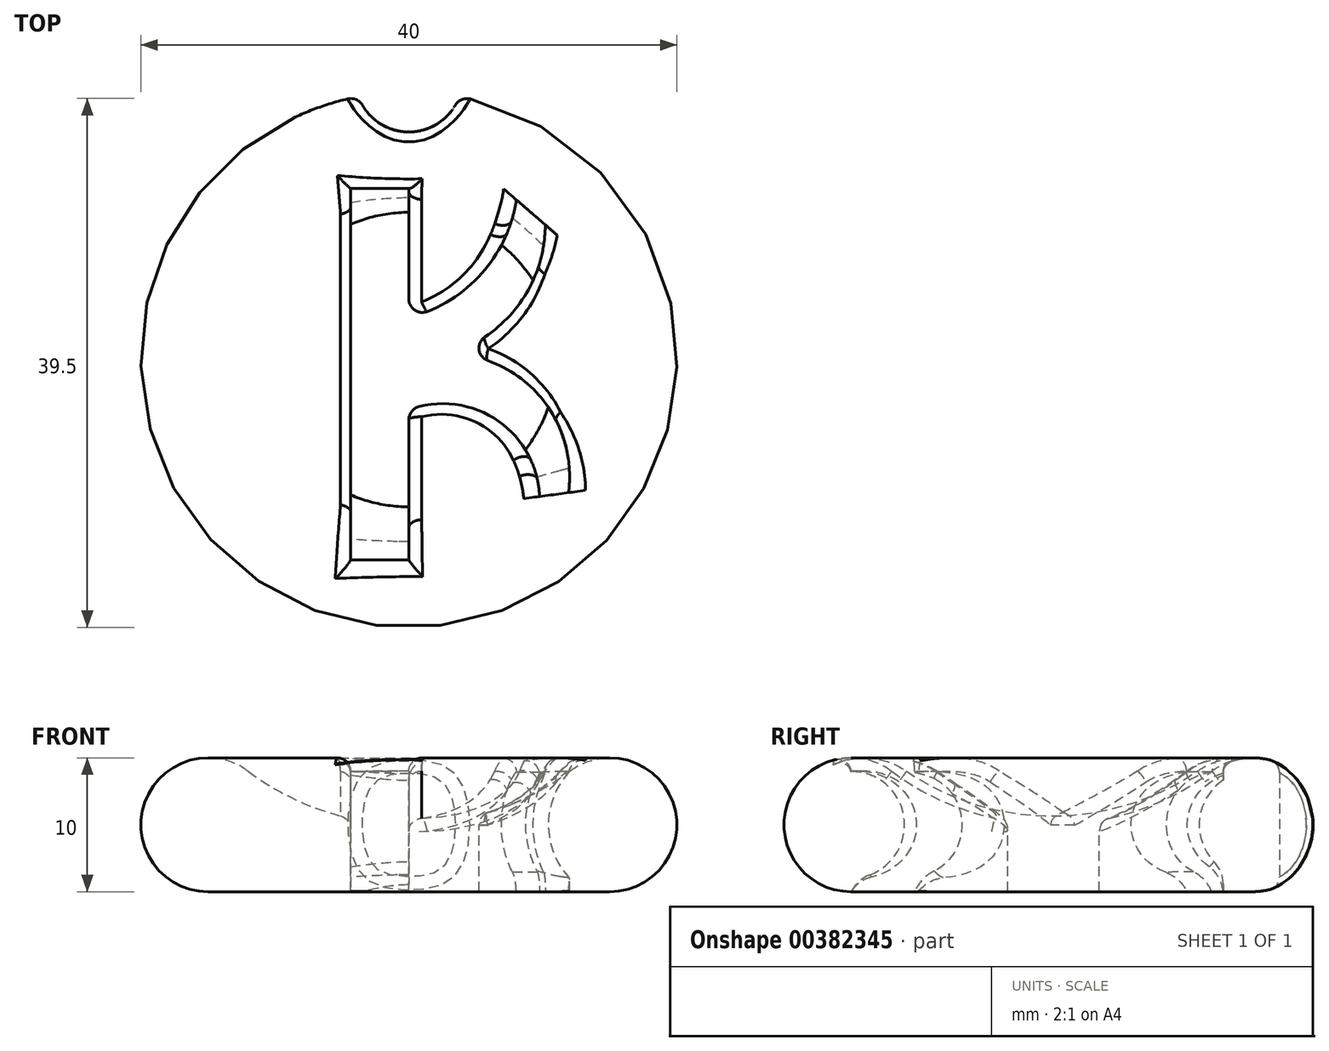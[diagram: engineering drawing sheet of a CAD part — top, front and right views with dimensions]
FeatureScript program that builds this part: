
annotation { "Feature Type Name" : "Feature", "Feature Type Description" : "" }
export const myFeature = defineFeature(function(context is Context, id is Id, definition is map)
    precondition{}
    {
        {
            var Q0;
            Q0=qCreatedBy(makeId("Front.planeOp"),FACE);
            var sketch = newSketch(context, id + "F0", { "sketchPlane" : qUnion([Q0])});
            skArc(sketch, "E0", {"start": v(-12, 9) * mm, "mid": v(-6.32, 6.03) * mm, "end": v(0, 5) * mm});
            skArc(sketch, "E1", {"start": v(-12, 9) * mm, "mid": v(-19.74, 6.58) * mm, "end": v(-15, 0) * mm});
            skLineSegment(sketch, "E2", {"start": v(-15, 0) * mm, "end": v(0, 0) * mm});
            skLineSegment(sketch, "E3", {"start": v(0, 0) * mm, "end": v(0, 5) * mm});
            skPoint(sketch, "E4.orphan", {"position": v(-410.72, 0) * mm});
            skSolve(sketch);
        }
        {
            var Q0;
            Q0=makeQuery(id+"F0.imprint","IMPRINT",FACE,{"disambiguationData":[TD([[makeQuery(id+"F0.imprint","IMPRINT",EDGE,{"derivedFrom":sQuery(id+"F0.wireOp",EDGE,"E0")}),-1.0]])]});
            var Q1;
            Q1=sQuery(id+"F0.wireOp",EDGE,"E3");
            revolve(context, id + "F1", {"entities" : qUnion([Q0]), "axis" : qUnion([Q1]), "revolveType" : RevolveType.FULL});
        }
        {
            var Q0;
            Q0=qCreatedBy(makeId("Top.planeOp"),FACE);
            cPlane(context, id + "F2", {"entities" : qUnion([Q0]), "cplaneType" : CPlaneType.OFFSET, "offset" : 15 * mm, "width" : 152.4 * mm, "height" : 152.4 * mm});
        }
        {
            var Q0;
            Q0=qCreatedBy(id+"F2.planeOp",FACE);
            var sketch = newSketch(context, id + "F3", { "sketchPlane" : qUnion([Q0])});
            skLineSegment(sketch, "E5", {"start": v(-4.35, 12.8) * mm, "end": v(0, 12.8) * mm});
            skLineSegment(sketch, "E6", {"start": v(0, 12.8) * mm, "end": v(0, 3.15) * mm});
            skLineSegment(sketch, "E7", {"start": v(0, -14.98) * mm, "end": v(-4.35, -14.98) * mm});
            skLineSegment(sketch, "E8", {"start": v(-4.35, -14.98) * mm, "end": v(-4.35, 12.8) * mm});
            skArc(sketch, "E9", {"start": v(0, 0) * mm, "mid": v(7.18, 2.92) * mm, "end": v(10.18, 10.06) * mm});
            skArc(sketch, "E10", {"start": v(0, 3.15) * mm, "mid": v(5.34, 6.33) * mm, "end": v(8.03, 11.93) * mm});
            skArc(sketch, "E11", {"start": v(11.91, -9.94) * mm, "mid": v(9.8, -2.77) * mm, "end": v(3.04, 0.44) * mm});
            skArc(sketch, "E12", {"start": v(9.75, -10.23) * mm, "mid": v(6.54, -4.49) * mm, "end": v(0, -3.75) * mm});
            skLineSegment(sketch, "E13", {"start": v(9.75, -10.23) * mm, "end": v(11.91, -9.94) * mm});
            skLineSegment(sketch, "E14", {"start": v(8.03, 11.93) * mm, "end": v(10.18, 10.06) * mm});
            skLineSegment(sketch, "E15.trimOffspring", {"start": v(0, -3.75) * mm, "end": v(0, -14.98) * mm});
            skSolve(sketch);
        }
        {
            var Q0;
            Q0 = qSketchRegion(id + "F3", true);
            extrude(context, id + "F4", {"entities" : qUnion([Q0]), "operationType" : NewBodyOperationType.REMOVE, "oppositeDirection" : true, "depth" : 25.4 * mm});
        }
        {
            var Q0;
            Q0=qCreatedBy(makeId("Front.planeOp"),FACE);
            var sketch = newSketch(context, id + "F5", { "sketchPlane" : qUnion([Q0])});
            skCircle(sketch, "E16", {"center": v(-15, 5) * mm, "radius": 4 * mm});
            skSolve(sketch);
        }
        {
            var Q0;
            Q0 = qSketchRegion(id + "F5", true);
            var Q1;
            Q1=sQuery(id+"F0.wireOp",EDGE,"E3");
            revolve(context, id + "F6", {"operationType" : NewBodyOperationType.ADD, "entities" : qUnion([Q0]), "axis" : qUnion([Q1]), "revolveType" : RevolveType.FULL});
        }
        {
            var Q0;
            Q0=qCreatedBy(makeId("Top.planeOp"),FACE);
            var sketch = newSketch(context, id + "F7", { "sketchPlane" : qUnion([Q0])});
            skCircle(sketch, "E17", {"center": v(0, 21) * mm, "radius": 4 * mm});
            skSolve(sketch);
        }
        {
            var Q0;
            Q0=makeQuery(id+"F7.imprint","IMPRINT",FACE,{"disambiguationData":[TD([[makeQuery(id+"F7.imprint","IMPRINT",EDGE,{"derivedFrom":sQuery(id+"F7.wireOp",EDGE,"E17")}),1.0]])]});
            extrude(context, id + "F8", {"entities" : qUnion([Q0]), "operationType" : NewBodyOperationType.REMOVE, "depth" : 25.15 * mm});
        }
        {
            var Q0;
            Q0=makeQuery(id+"F8.boolean.opBoolean","INTERSECT",EDGE,{"derivedFrom":[makeQuery(id+"F1.opRevolve","SWEPT_FACE",FACE,{"disambiguationData":[OSD([sQuery(id+"F0.wireOp",EDGE,"E1")])]}),makeQuery(id+"F8.opExtrude","SWEPT_FACE",FACE,{"disambiguationData":[OSD([sQuery(id+"F7.wireOp",EDGE,"E17")])]})]});
            fillet(context, id + "F9", {"entities" : qUnion([Q0]), "radius" : 1 * mm, "tangentPropagation" : true, "allowEdgeOverflow" : false});
        }
        {
            var Q0;
            Q0=makeQuery(id+"F6.boolean.opBoolean","INTERSECT",EDGE,{"disambiguationData":[OD(1.0)],"derivedFrom":[makeQuery(id+"F4.boolean.opBoolean","COPY",FACE,{"derivedFrom":makeQuery(id+"F4.opExtrude","SWEPT_FACE",FACE,{"disambiguationData":[OSD([sQuery(id+"F3.wireOp",EDGE,"E14")])]})}),makeQuery(id+"F6.opRevolve","SWEPT_FACE",FACE,{"disambiguationData":[OSD([sQuery(id+"F5.wireOp",EDGE,"E16")])]})]});
            var Q1;
            Q1=makeQuery(id+"F6.boolean.opBoolean","INTERSECT",EDGE,{"disambiguationData":[OD(0.0)],"derivedFrom":[makeQuery(id+"F4.boolean.opBoolean","COPY",FACE,{"derivedFrom":makeQuery(id+"F4.opExtrude","SWEPT_FACE",FACE,{"disambiguationData":[OSD([sQuery(id+"F3.wireOp",EDGE,"E13")])]})}),makeQuery(id+"F6.opRevolve","SWEPT_FACE",FACE,{"disambiguationData":[OSD([sQuery(id+"F5.wireOp",EDGE,"E16")])]})]});
            var Q2;
            Q2=makeQuery(id+"F6.boolean.opBoolean","INTERSECT",EDGE,{"disambiguationData":[OD(0.0)],"derivedFrom":[makeQuery(id+"F4.boolean.opBoolean","COPY",FACE,{"derivedFrom":makeQuery(id+"F4.opExtrude","SWEPT_FACE",FACE,{"disambiguationData":[OSD([sQuery(id+"F3.wireOp",EDGE,"E7")])]})}),makeQuery(id+"F6.opRevolve","SWEPT_FACE",FACE,{"disambiguationData":[OSD([sQuery(id+"F5.wireOp",EDGE,"E16")])]})]});
            var Q3;
            Q3=makeQuery(id+"F6.boolean.opBoolean","INTERSECT",EDGE,{"disambiguationData":[OD(1.0)],"derivedFrom":[makeQuery(id+"F4.boolean.opBoolean","COPY",FACE,{"derivedFrom":makeQuery(id+"F4.opExtrude","SWEPT_FACE",FACE,{"disambiguationData":[OSD([sQuery(id+"F3.wireOp",EDGE,"E5")])]})}),makeQuery(id+"F6.opRevolve","SWEPT_FACE",FACE,{"disambiguationData":[OSD([sQuery(id+"F5.wireOp",EDGE,"E16")])]})]});
            fillet(context, id + "F10", {"entities" : qUnion([Q0, Q1, Q2, Q3]), "radius" : 2.5 * mm, "tangentPropagation" : true, "allowEdgeOverflow" : false});
        }
        {
            var Q0;
            Q0=makeQuery(id+"F4.boolean.opBoolean","INTERSECT",EDGE,{"derivedFrom":[makeQuery(id+"F1.opRevolve","SWEPT_FACE",FACE,{"disambiguationData":[OSD([sQuery(id+"F0.wireOp",EDGE,"E1")])]}),makeQuery(id+"F4.opExtrude","SWEPT_FACE",FACE,{"disambiguationData":[OSD([sQuery(id+"F3.wireOp",EDGE,"E12")])]})]});
            var Q1;
            Q1=makeQuery(id+"F4.boolean.opBoolean","INTERSECT",EDGE,{"derivedFrom":[makeQuery(id+"F1.opRevolve","SWEPT_FACE",FACE,{"disambiguationData":[OSD([sQuery(id+"F0.wireOp",EDGE,"E0")])]}),makeQuery(id+"F4.opExtrude","SWEPT_FACE",FACE,{"disambiguationData":[OSD([sQuery(id+"F3.wireOp",EDGE,"E15.trimOffspring")])]})]});
            var Q2;
            Q2=makeQuery(id+"F4.boolean.opBoolean","INTERSECT",EDGE,{"derivedFrom":[makeQuery(id+"F1.opRevolve","SWEPT_FACE",FACE,{"disambiguationData":[OSD([sQuery(id+"F0.wireOp",EDGE,"E0")])]}),makeQuery(id+"F4.opExtrude","SWEPT_FACE",FACE,{"disambiguationData":[OSD([sQuery(id+"F3.wireOp",EDGE,"E11")])]})]});
            var Q3;
            Q3=makeQuery(id+"F4.boolean.opBoolean","INTERSECT",EDGE,{"derivedFrom":[makeQuery(id+"F1.opRevolve","SWEPT_FACE",FACE,{"disambiguationData":[OSD([sQuery(id+"F0.wireOp",EDGE,"E0")])]}),makeQuery(id+"F4.opExtrude","SWEPT_FACE",FACE,{"disambiguationData":[OSD([sQuery(id+"F3.wireOp",EDGE,"E9")])]})]});
            var Q4;
            Q4=makeQuery(id+"F4.boolean.opBoolean","INTERSECT",EDGE,{"derivedFrom":[makeQuery(id+"F1.opRevolve","SWEPT_FACE",FACE,{"disambiguationData":[OSD([sQuery(id+"F0.wireOp",EDGE,"E0")])]}),makeQuery(id+"F4.opExtrude","SWEPT_FACE",FACE,{"disambiguationData":[OSD([sQuery(id+"F3.wireOp",EDGE,"E10")])]})]});
            var Q5;
            Q5=makeQuery(id+"F4.boolean.opBoolean","INTERSECT",EDGE,{"derivedFrom":[makeQuery(id+"F1.opRevolve","SWEPT_FACE",FACE,{"disambiguationData":[OSD([sQuery(id+"F0.wireOp",EDGE,"E0")])]}),makeQuery(id+"F4.opExtrude","SWEPT_FACE",FACE,{"disambiguationData":[OSD([sQuery(id+"F3.wireOp",EDGE,"E6")])]})]});
            var Q6;
            Q6=makeQuery(id+"F4.boolean.opBoolean","INTERSECT",EDGE,{"derivedFrom":[makeQuery(id+"F1.opRevolve","SWEPT_FACE",FACE,{"disambiguationData":[OSD([sQuery(id+"F0.wireOp",EDGE,"E0")])]}),makeQuery(id+"F4.opExtrude","SWEPT_FACE",FACE,{"disambiguationData":[OSD([sQuery(id+"F3.wireOp",EDGE,"E8")])]})]});
            var Q7;
            Q7=makeQuery(id+"F4.boolean.opBoolean","INTERSECT",EDGE,{"derivedFrom":[makeQuery(id+"F1.opRevolve","SWEPT_FACE",FACE,{"disambiguationData":[OSD([sQuery(id+"F0.wireOp",EDGE,"E1")])]}),makeQuery(id+"F4.opExtrude","SWEPT_FACE",FACE,{"disambiguationData":[OSD([sQuery(id+"F3.wireOp",EDGE,"E5")])]})]});
            var Q8;
            Q8=makeQuery(id+"F4.boolean.opBoolean","INTERSECT",EDGE,{"disambiguationData":[OD(0.0)],"derivedFrom":[makeQuery(id+"F1.opRevolve","SWEPT_FACE",FACE,{"disambiguationData":[OSD([sQuery(id+"F0.wireOp",EDGE,"E1")])]}),makeQuery(id+"F4.opExtrude","SWEPT_FACE",FACE,{"disambiguationData":[OSD([sQuery(id+"F3.wireOp",EDGE,"E7")])]})]});
            var Q9;
            Q9=makeQuery(id+"F4.boolean.opBoolean","COPY",EDGE,{"derivedFrom":makeQuery(id+"F4.opExtrude","SWEPT_EDGE",EDGE,{"disambiguationData":[OSD([sQuery(id+"F3.wireOp",EDGE,"E9"),sQuery(id+"F3.wireOp",EDGE,"E11")])]})});
            var Q10;
            Q10=makeQuery(id+"F4.boolean.opBoolean","COPY",EDGE,{"derivedFrom":makeQuery(id+"F4.opExtrude","SWEPT_EDGE",EDGE,{"disambiguationData":[OSD([sQuery(id+"F3.wireOp",EDGE,"E12"),sQuery(id+"F3.wireOp",EDGE,"E15.trimOffspring")])]})});
            var Q11;
            Q11=makeQuery(id+"F4.boolean.opBoolean","COPY",EDGE,{"derivedFrom":makeQuery(id+"F4.opExtrude","SWEPT_EDGE",EDGE,{"disambiguationData":[OSD([sQuery(id+"F3.wireOp",EDGE,"E6"),sQuery(id+"F3.wireOp",EDGE,"E10")])]})});
            fillet(context, id + "F11", {"entities" : qUnion([Q0, Q1, Q2, Q3, Q4, Q5, Q6, Q7, Q8, Q9, Q10, Q11]), "radius" : 1 * mm, "tangentPropagation" : true, "allowEdgeOverflow" : false});
        }
    });
